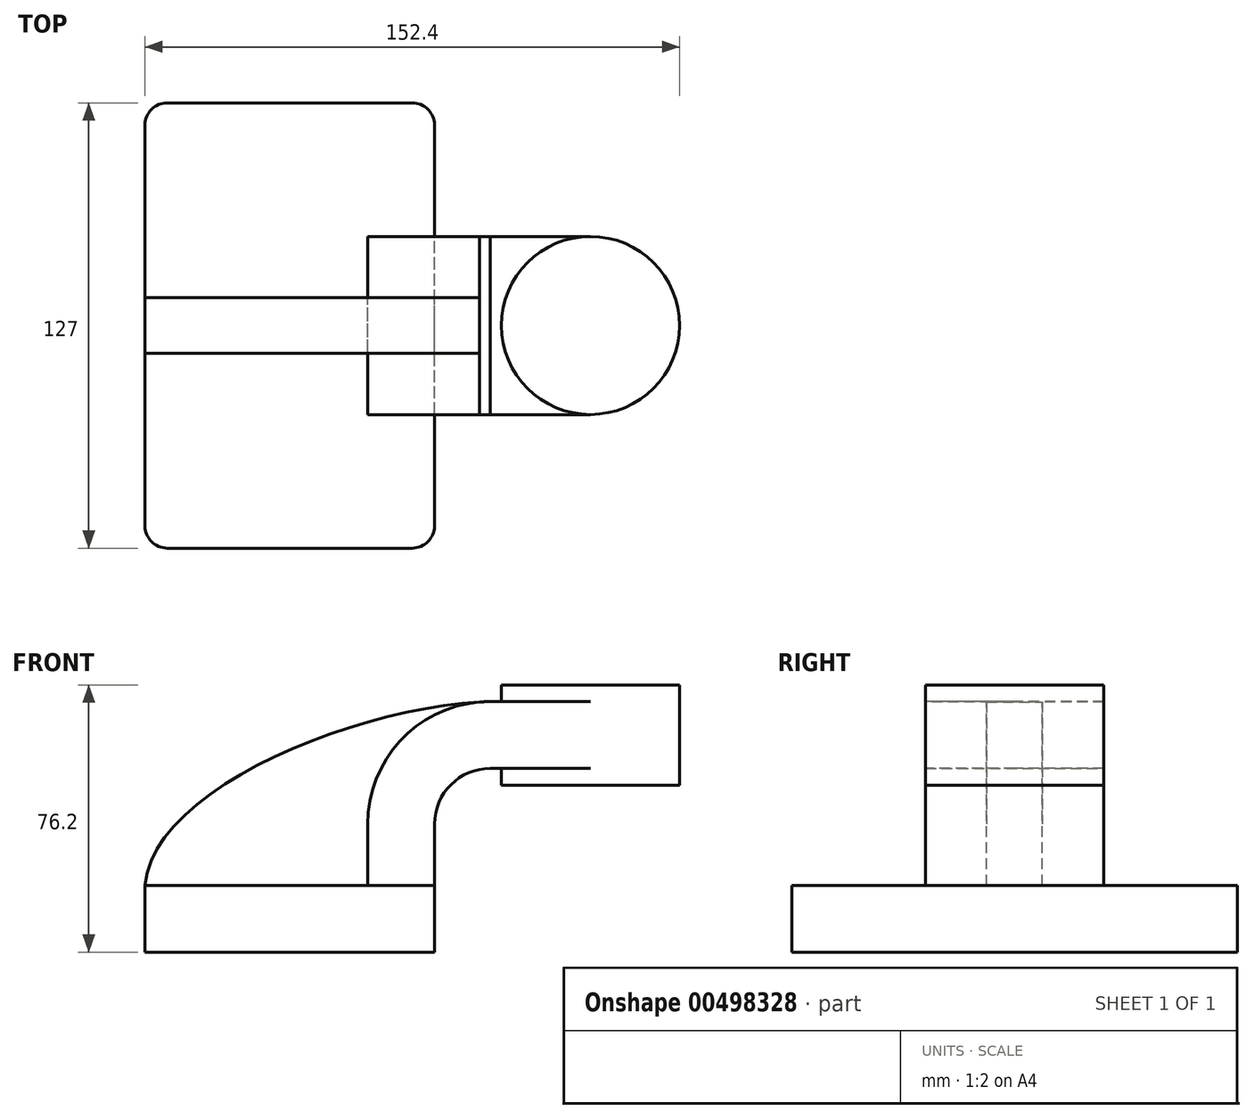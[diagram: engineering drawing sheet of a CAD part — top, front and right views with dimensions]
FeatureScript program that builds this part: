
annotation { "Feature Type Name" : "Feature", "Feature Type Description" : "" }
export const myFeature = defineFeature(function(context is Context, id is Id, definition is map)
    precondition{}
    {
        {
            var Q0;
            Q0=qCreatedBy(makeId("Front.planeOp"),FACE);
            var sketch = newSketch(context, id + "F0", { "sketchPlane" : qUnion([Q0])});
            skLineSegment(sketch, "E0.bottom", {"start": v(-47.5, 8.34) * mm, "end": v(35.05, 8.34) * mm});
            skLineSegment(sketch, "E0.top", {"start": v(-47.5, -10.71) * mm, "end": v(35.05, -10.71) * mm});
            skLineSegment(sketch, "E0.left", {"start": v(-47.5, 8.34) * mm, "end": v(-47.5, -10.71) * mm});
            skLineSegment(sketch, "E0.right", {"start": v(35.05, 8.34) * mm, "end": v(35.05, -10.71) * mm});
            skLineSegment(sketch, "E1", {"start": v(35.05, 8.34) * mm, "end": v(35.05, 25.81) * mm});
            skArc(sketch, "E2", {"start": v(50.93, 41.69) * mm, "mid": v(39.7, 37.04) * mm, "end": v(35.05, 25.81) * mm});
            skLineSegment(sketch, "E3.bottom", {"start": v(54.1, 65.49) * mm, "end": v(104.9, 65.49) * mm});
            skLineSegment(sketch, "E3.top", {"start": v(54.1, 36.91) * mm, "end": v(104.9, 36.91) * mm});
            skLineSegment(sketch, "E3.left", {"start": v(54.1, 65.49) * mm, "end": v(54.1, 36.91) * mm});
            skLineSegment(sketch, "E3.right", {"start": v(104.9, 65.49) * mm, "end": v(104.9, 36.91) * mm});
            skLineSegment(sketch, "E4", {"start": v(50.93, 41.69) * mm, "end": v(79.5, 41.69) * mm});
            skPoint(sketch, "E4.endSnap0", {"position": v(79.5, 36.91) * mm});
            skLineSegment(sketch, "E5.0", {"start": v(50.93, 60.74) * mm, "end": v(79.5, 60.74) * mm});
            skArc(sketch, "E5.1", {"start": v(50.93, 60.74) * mm, "mid": v(26.23, 50.5) * mm, "end": v(16, 25.81) * mm});
            skLineSegment(sketch, "E5.2", {"start": v(16, 8.38) * mm, "end": v(16, 25.81) * mm});
            skLineSegment(sketch, "E6", {"start": v(79.5, 60.74) * mm, "end": v(79.5, 41.69) * mm});
            skLineSegment(sketch, "E7", {"start": v(16, 8.38) * mm, "end": v(35.05, 8.34) * mm});
            skFitSpline(sketch, "E8", {"points": [v(-47.5, 8.34) * mm, v(50.93, 60.74) * mm], "startDerivative": vector(6.86, 83.2) * mm, "endDerivative": vector(112.4, 3.14) * mm});
            skLineSegment(sketch, "E9", {"start": v(79.5, 36.91) * mm, "end": v(79.5, 41.69) * mm});
            skLineSegment(sketch, "E10", {"start": v(79.5, 60.74) * mm, "end": v(79.5, 65.49) * mm});
            skSolve(sketch);
        }
        {
            var Q0;
            Q0=makeQuery(id+"F0.imprint","IMPRINT",FACE,{"disambiguationData":[TD([[makeQuery(id+"F0.imprint","IMPRINT",EDGE,{"derivedFrom":sQuery(id+"F0.wireOp",EDGE,"E0.bottom")}),-1.0]])]});
            extrude(context, id + "F1", {"entities" : qUnion([Q0]), "endBound" : BoundingType.SYMMETRIC, "depth" : 127 * mm});
        }
        {
            var Q0;
            Q0=makeQuery(id+"F0.imprint","IMPRINT",FACE,{"disambiguationData":[TD([[makeQuery(id+"F0.imprint","IMPRINT",EDGE,{"derivedFrom":sQuery(id+"F0.wireOp",EDGE,"E1")}),1.0]])]});
            extrude(context, id + "F2", {"entities" : qUnion([Q0]), "endBound" : BoundingType.SYMMETRIC, "depth" : 50.8 * mm});
        }
        {
            var Q0;
            {var subQ4=sQuery(id+"F0.wireOp",EDGE,"E0.bottom");Q0=makeQuery(id+"F0.imprint","IMPRINT",FACE,{"disambiguationData":[TD([[makeQuery(id+"F0.imprint","IMPRINT",EDGE,{"derivedFrom":subQ4}),1.0]])]});}
            extrude(context, id + "F3", {"entities" : qUnion([Q0]), "endBound" : BoundingType.SYMMETRIC, "depth" : 15.88 * mm});
        }
        {
            var Q0;
            {var subQ5=sQuery(id+"F0.wireOp",EDGE,"E6");Q0=makeQuery(id+"F0.imprint","IMPRINT",FACE,{"disambiguationData":[TD([[makeQuery(id+"F0.imprint","IMPRINT",EDGE,{"derivedFrom":subQ5}),-1.0]])]});}
            extrude(context, id + "F4", {"entities" : qUnion([Q0]), "operationType" : NewBodyOperationType.ADD, "endBound" : BoundingType.SYMMETRIC, "depth" : 50.8 * mm});
        }
        {
            var Q0;
            {var subQ0=sQuery(id+"F0.wireOp",EDGE,"E3.right");Q0=makeQuery(id+"F0.imprint","IMPRINT",FACE,{"disambiguationData":[TD([[makeQuery(id+"F0.imprint","IMPRINT",EDGE,{"derivedFrom":subQ0}),-1.0]])]});}
            var Q1;
            Q1=sQuery(id+"F0.wireOp",EDGE,"E9");
            revolve(context, id + "F5", {"operationType" : NewBodyOperationType.ADD, "entities" : qUnion([Q0]), "axis" : qUnion([Q1]), "revolveType" : RevolveType.FULL});
        }
        {
            var Q0;
            Q0=makeQuery(id+"F1.opExtrude","CAP_EDGE",EDGE,{"disambiguationData":[OSD([sQuery(id+"F0.wireOp",EDGE,"E0.left")])],"isStart":false});
            var Q1;
            Q1=makeQuery(id+"F1.opExtrude","CAP_EDGE",EDGE,{"disambiguationData":[OSD([sQuery(id+"F0.wireOp",EDGE,"E0.right")])],"isStart":false});
            var Q2;
            Q2=makeQuery(id+"F1.opExtrude","CAP_EDGE",EDGE,{"disambiguationData":[OSD([sQuery(id+"F0.wireOp",EDGE,"E0.right")])],"isStart":true});
            var Q3;
            Q3=makeQuery(id+"F1.opExtrude","CAP_EDGE",EDGE,{"disambiguationData":[OSD([sQuery(id+"F0.wireOp",EDGE,"E0.left")])],"isStart":true});
            fillet(context, id + "F6", {"entities" : qUnion([Q0, Q1, Q2, Q3]), "radius" : 6.35 * mm, "tangentPropagation" : true, "allowEdgeOverflow" : false});
        }
    });
